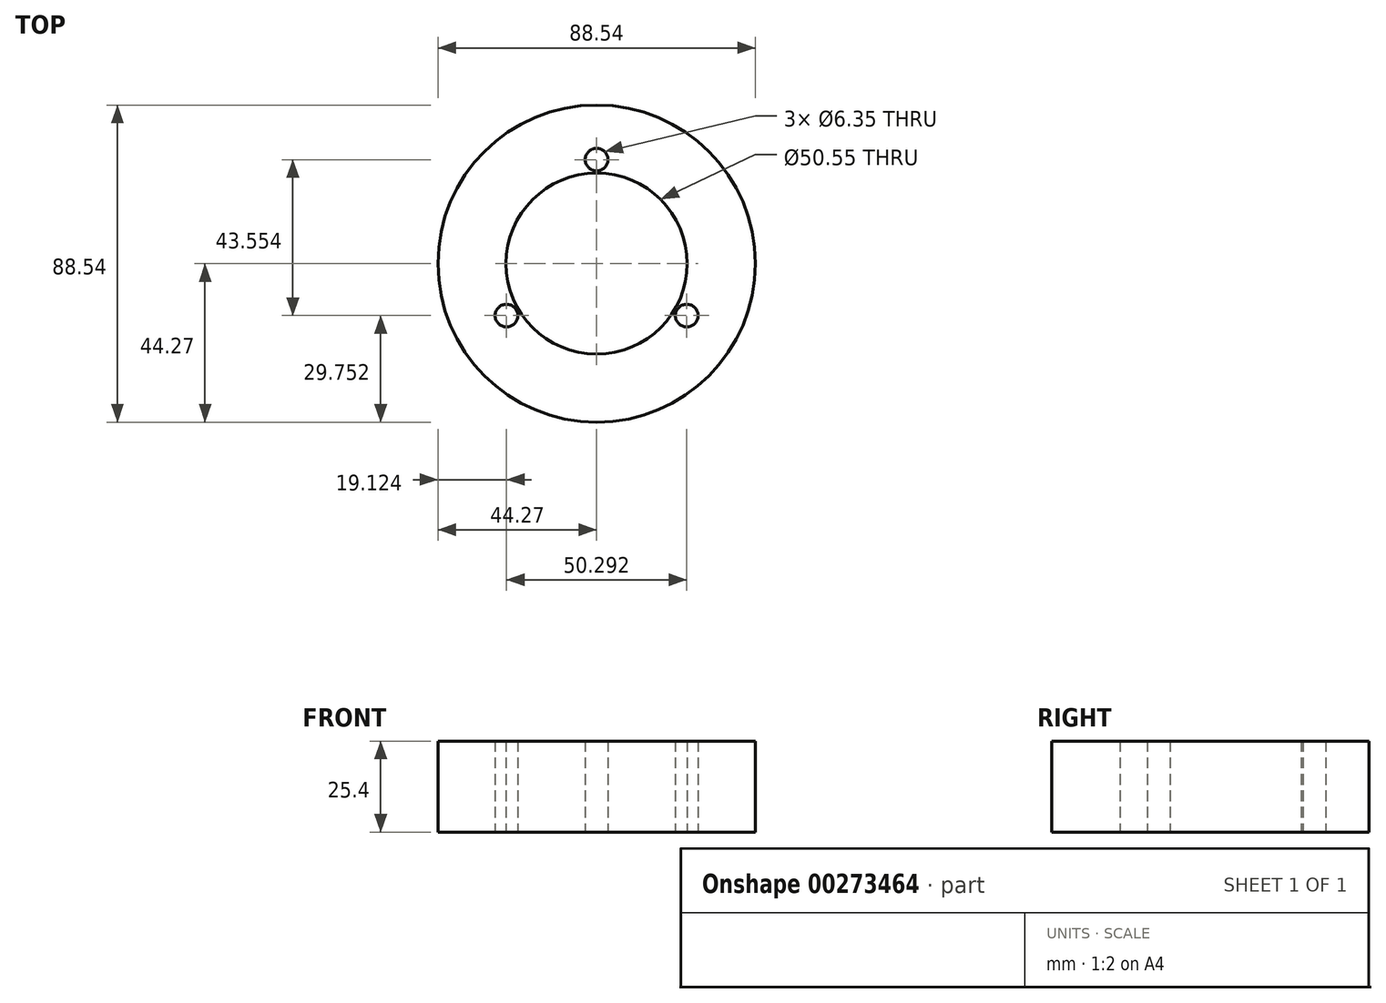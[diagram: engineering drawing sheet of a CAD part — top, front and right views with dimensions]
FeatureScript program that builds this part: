
annotation { "Feature Type Name" : "Feature", "Feature Type Description" : "" }
export const myFeature = defineFeature(function(context is Context, id is Id, definition is map)
    precondition{}
    {
        {
            var Q0;
            Q0=qCreatedBy(makeId("Top.planeOp"),FACE);
            var sketch = newSketch(context, id + "F0", { "sketchPlane" : qUnion([Q0])});
            skCircle(sketch, "E0", {"center": v(0, 0) * mm, "radius": 44.27 * mm});
            skCircle(sketch, "E1", {"center": v(0, 0) * mm, "radius": 29.04 * mm, "construction": true});
            skCircle(sketch, "E2", {"center": v(0, 29.04) * mm, "radius": 3.17 * mm});
            skCircle(sketch, "E3", {"center": v(-25.15, -14.52) * mm, "radius": 3.18 * mm});
            skCircle(sketch, "E4", {"center": v(25.15, -14.52) * mm, "radius": 3.18 * mm});
            skLineSegment(sketch, "E5", {"start": v(0, 0) * mm, "end": v(-25.15, -14.52) * mm, "construction": true});
            skLineSegment(sketch, "E6", {"start": v(0, 0) * mm, "end": v(25.15, -14.52) * mm, "construction": true});
            skLineSegment(sketch, "E7", {"start": v(0, 0) * mm, "end": v(0, 29.04) * mm, "construction": true});
            skCircle(sketch, "E8", {"center": v(0, 0) * mm, "radius": 25.27 * mm});
            skSolve(sketch);
        }
        {
            var Q0;
            Q0 = qSketchRegion(id + "F0", true);
            extrude(context, id + "F1", {"entities" : qUnion([Q0]), "depth" : 25.4 * mm});
        }
    });
